# Revit family: WWW_A3-Flat-Arch-2090-FAB6
name_source: partatom
category: Windows
revit_build: Autodesk Revit 2016 (Build: 20150220_1215(x64)
units: mm (PartAtom-declared; Revit-internal decimal feet)

## family parameters
Always vertical = Yes
Cut with Voids When Loaded = No
Host = Wall
Room Calculation Point = No
Shared = No

## types (4) — shared parameters
Assembly Code = B2020130
Frame Material = Wood- Timber
Head Height = 2300 mm
Manufacturer = AC Shopfitters (Windows)
Manufacturer Code = FAB6
Model = Flat Arch
Type Comments = Series iv Frame Profile
URL = www.acdoors.co.za
Wall Closure = By host

## per-type parameters (varying)
| type | Default Sill Height | Height | Width |
| 1888 x 1500 FAB6 | 412 mm  [stored 1.35171 ft] | 1888 mm | 1500 mm  [stored 4.92126 ft] |
| 2090 x 1116 FAB6 | 210 mm  [stored 0.688976 ft] | 2090 mm  [stored 6.85696 ft] | 1116 mm  [stored 3.66142 ft] |
| 2090 x 1500 FAB6 | 210 mm  [stored 0.688976 ft] | 2090 mm  [stored 6.85696 ft] | 1500 mm  [stored 4.92126 ft] |
| 1888 x 1116 FAB6 | 412 mm  [stored 1.35171 ft] | 1888 mm | 1116 mm  [stored 3.66142 ft] |

note: [stored X ft] marks values corroborated as IEEE doubles in the binary element streams (Revit-internal decimal feet)

## geometry (parser evidence)
native form markers: Sweep x5
no freeform markers — native parametric forms only
